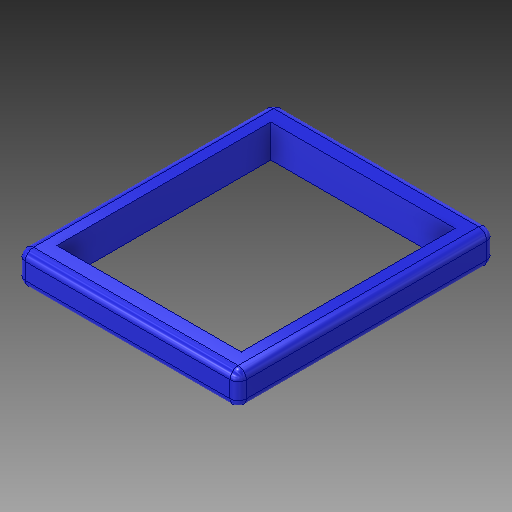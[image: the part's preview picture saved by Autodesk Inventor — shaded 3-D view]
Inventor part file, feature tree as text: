
AUTODESK INVENTOR PART (.ipt)
format: ipt  version: 2017 SP1 (Build 210196100, 196)  size: 136,192 bytes
history: native  units: in
note: dims shown in document units (in); Inventor stores cm internally (conversion verified against a paired STEP export)
features: extrude x1, fillet x1, sketch x1
ambient origin geometry x8: Origin, YZ Plane, XZ Plane, XY Plane, X Axis, Y Axis, Z Axis, Center Point
bodies: Solid1 (feature_tree)
feature tree (3):
  extrude  "Extrusion1"  Depth=28.0in
  fillet  "Fillet1"  Radius=3.25in
  sketch  "Sketch1"  dims[d0=32.5in d1=28.0in d2=3.25in d3=5.0in d4=0.0in d5=1.25in]
